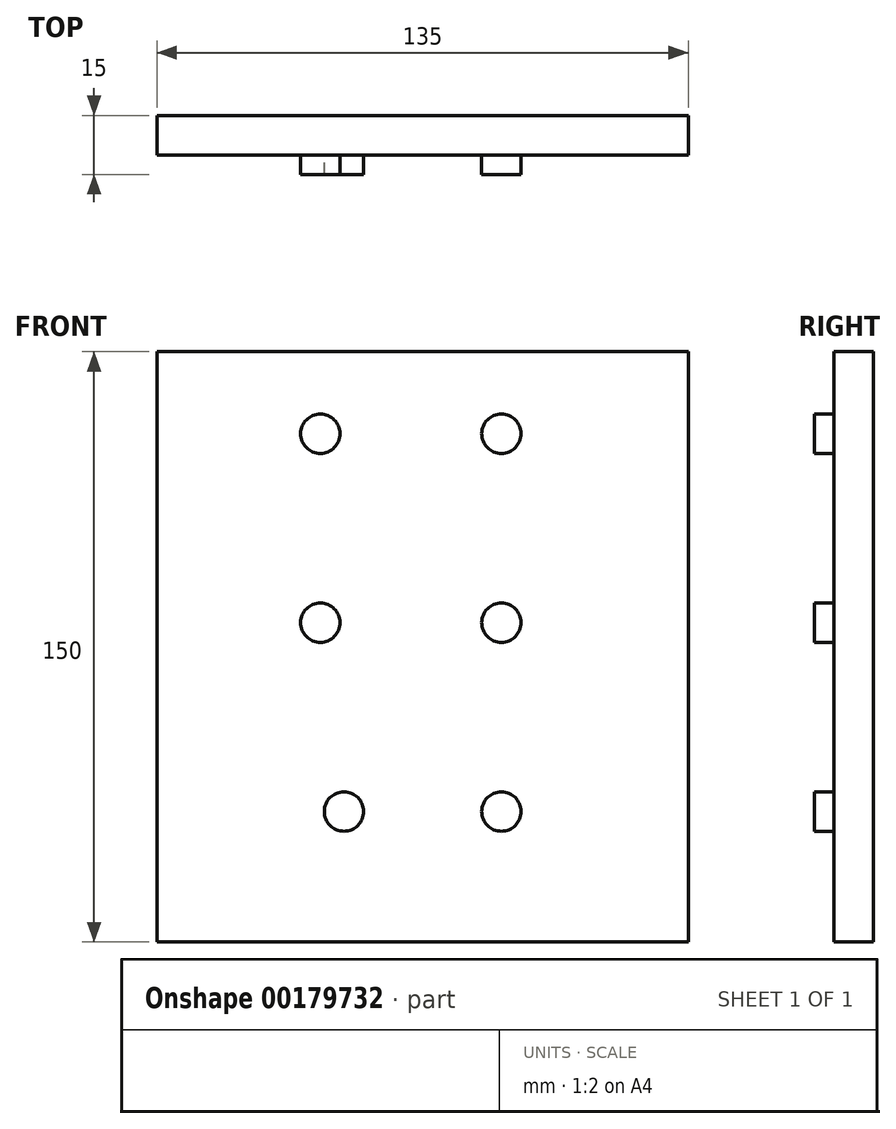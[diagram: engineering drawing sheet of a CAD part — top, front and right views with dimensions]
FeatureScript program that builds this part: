
annotation { "Feature Type Name" : "Feature", "Feature Type Description" : "" }
export const myFeature = defineFeature(function(context is Context, id is Id, definition is map)
    precondition{}
    {
        {
            var Q0;
            Q0=qCreatedBy(makeId("Front.planeOp"),FACE);
            var sketch = newSketch(context, id + "F0", { "sketchPlane" : qUnion([Q0])});
            skLineSegment(sketch, "E0.bottom", {"start": v(67.5, -75) * mm, "end": v(-67.5, -75) * mm});
            skLineSegment(sketch, "E0.top", {"start": v(67.5, 75) * mm, "end": v(-67.5, 75) * mm});
            skLineSegment(sketch, "E0.left", {"start": v(67.5, -75) * mm, "end": v(67.5, 75) * mm});
            skLineSegment(sketch, "E0.right", {"start": v(-67.5, -75) * mm, "end": v(-67.5, 75) * mm});
            skPoint(sketch, "E0.middle", {"position": v(0, 0) * mm});
            skSolve(sketch);
        }
        {
            var Q0;
            Q0=makeQuery(id+"F0.imprint","IMPRINT",FACE,{"disambiguationData":[TD([[makeQuery(id+"F0.imprint","IMPRINT",EDGE,{"derivedFrom":sQuery(id+"F0.wireOp",EDGE,"E0.bottom")}),-1.0]])]});
            extrude(context, id + "F1", {"entities" : qUnion([Q0]), "oppositeDirection" : true, "depth" : 10 * mm});
        }
        {
            var Q0;
            Q0=makeQuery(id+"F1.opExtrude","CAP_FACE",FACE,{"disambiguationData":[OSD([sQuery(id+"F0.wireOp",EDGE,"E0.bottom"),sQuery(id+"F0.wireOp",EDGE,"E0.top"),sQuery(id+"F0.wireOp",EDGE,"E0.left"),sQuery(id+"F0.wireOp",EDGE,"E0.right")])],"isStart":true});
            var sketch = newSketch(context, id + "F2", { "sketchPlane" : qUnion([Q0])});
            skCircle(sketch, "E1", {"center": v(-20, -41.86) * mm, "radius": 5 * mm});
            skCircle(sketch, "E2", {"center": v(20, -41.86) * mm, "radius": 5 * mm});
            skCircle(sketch, "E3", {"center": v(20, 6.14) * mm, "radius": 5 * mm});
            skCircle(sketch, "E4", {"center": v(-26, 6.14) * mm, "radius": 5 * mm});
            skCircle(sketch, "E5", {"center": v(-26, 54.14) * mm, "radius": 5 * mm});
            skCircle(sketch, "E6", {"center": v(20, 54.14) * mm, "radius": 5 * mm});
            skSolve(sketch);
        }
        {
            var Q0;
            Q0 = qSketchRegion(id + "F2", true);
            extrude(context, id + "F3", {"entities" : qUnion([Q0]), "operationType" : NewBodyOperationType.ADD, "depth" : 5 * mm});
        }
    });
